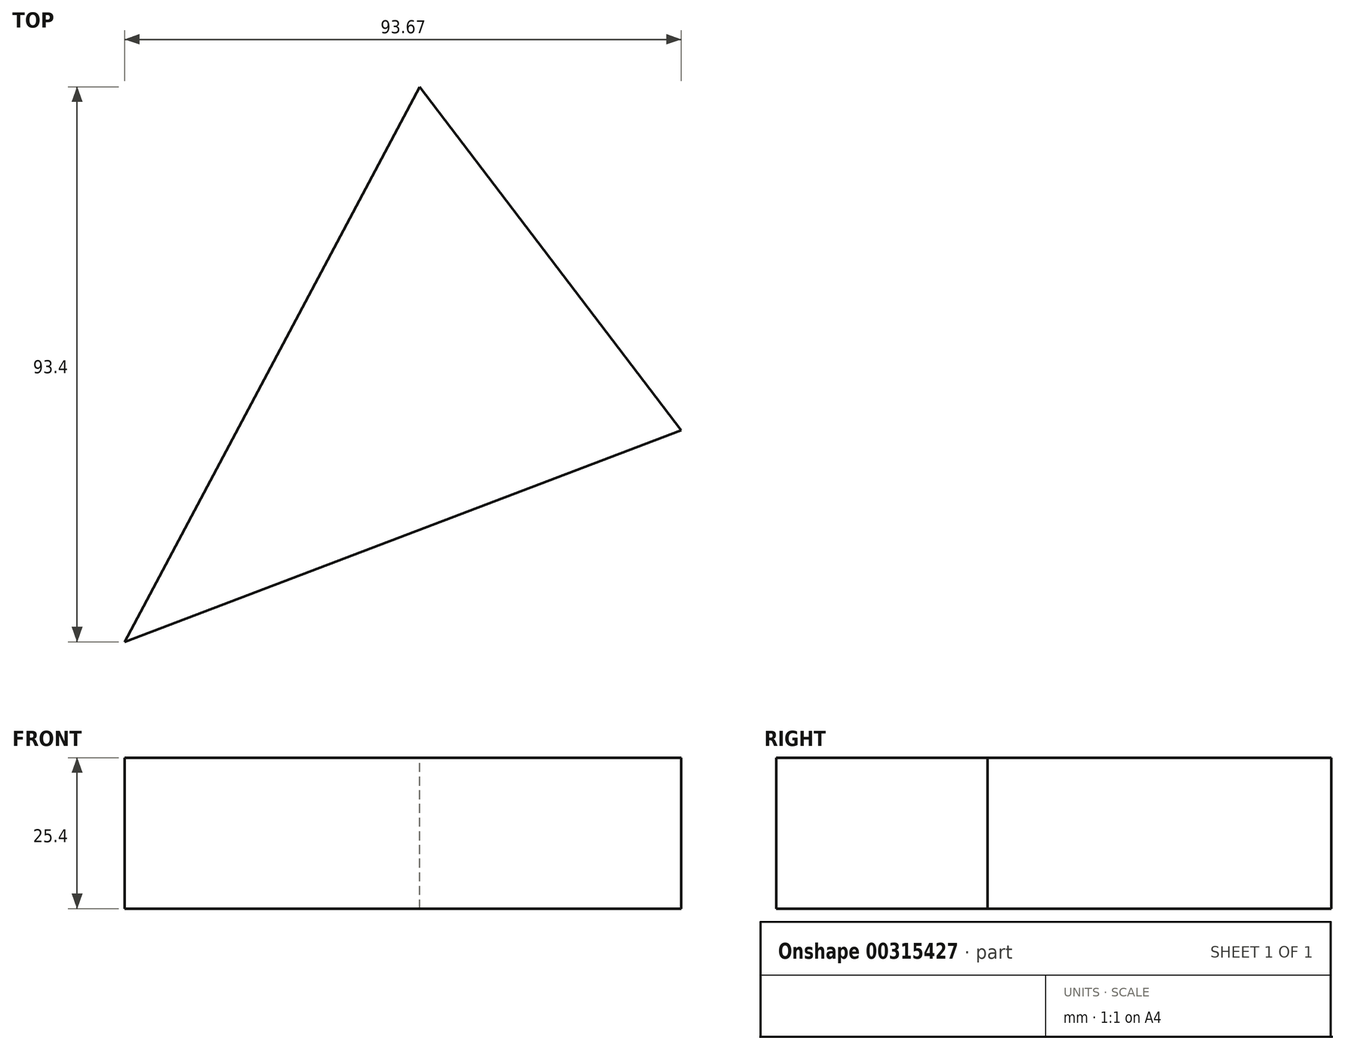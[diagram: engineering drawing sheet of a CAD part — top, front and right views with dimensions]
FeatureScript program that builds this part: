
annotation { "Feature Type Name" : "Feature", "Feature Type Description" : "" }
export const myFeature = defineFeature(function(context is Context, id is Id, definition is map)
    precondition{}
    {
        {
            var Q0;
            Q0=qCreatedBy(makeId("Top.planeOp"),FACE);
            var sketch = newSketch(context, id + "F0", { "sketchPlane" : qUnion([Q0])});
            skLineSegment(sketch, "E0", {"start": v(23.85, -11.66) * mm, "end": v(-20.17, 46.15) * mm});
            skLineSegment(sketch, "E1", {"start": v(-20.17, 46.15) * mm, "end": v(-69.82, -47.25) * mm});
            skLineSegment(sketch, "E2", {"start": v(-69.82, -47.25) * mm, "end": v(23.85, -11.66) * mm});
            skSolve(sketch);
        }
        {
            var Q0;
            Q0=makeQuery(id+"F0.imprint","IMPRINT",FACE,{"disambiguationData":[TD([[makeQuery(id+"F0.imprint","IMPRINT",EDGE,{"derivedFrom":sQuery(id+"F0.wireOp",EDGE,"E0")}),1.0]])]});
            extrude(context, id + "F1", {"entities" : qUnion([Q0]), "oppositeDirection" : true, "depth" : 25.4 * mm});
        }
    });
